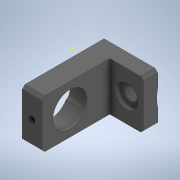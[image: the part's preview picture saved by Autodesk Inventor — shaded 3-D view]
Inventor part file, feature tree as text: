
AUTODESK INVENTOR PART (.ipt)
format: ipt  version: 2020.4 (Build 244396000, 396)  size: 250,880 bytes
history: native  units: in
note: dims shown in document units (in); Inventor stores cm internally (conversion verified against a paired STEP export)
features: sketch x9, extrude x6, hole x3, other x2, chamfer x1
ambient origin geometry x8: Origin, YZ Plane, XZ Plane, XY Plane, X Axis, Y Axis, Z Axis, Center Point
bodies: Solid1 (feature_tree)
feature tree (21):
  other  "Table"
  other  "ADAPTER_fixed-mirror-BH19.05-D12.7"
  extrude  "Extrusion1"  Depth=0.3371in
  sketch  "Sketch2"  dims[d5=0.0in d6=0.6742in]
  extrude  "Extrusion2"  Depth=0.6742in
  extrude  "Extrusion3"  Depth=0.5567in
  extrude  "Extrusion4"  Depth=0.1201in
  hole  "Hole1"  [1 undecoded]
  sketch  "Sketch7"  dims[d15=0.1374in d16=0.0in]
  hole  "Hole2"  [1 undecoded]
  hole  "Hole4"  [1 undecoded]
  extrude  "Extrusion5"  Depth=0.75in
  chamfer  "Chamfer1"  Distance=0.0394in
  extrude  "Extrusion6"  Depth=0.3937in TaperAngle=0.0deg
  sketch  "Sketch10"  dims[d22=0.4774in d23=0.0394in d24=0.0in d25=0.1969in d26=0.0in d27=0.0in d28=0.2362in d29=0.1772in d30=0.2362in d31=0.315in d32=0.0591in d33=90.0deg d34=0.1614in d35=0.0in d36=0.0in d37=0.0in d38=0.1969in d39=0.1969in d40=0.0827in d41=0.2362in d42=0.3126in d43=0.1642in d44=90.0deg d45=0.0827in d46=0.0in d47=0.1378in d48=0.0in d56=0.0849in d57=0.224in d58=0.1575in d59=0.0787in d60=90.0deg d61=0.3492in d62=0.0in d63=0.0413in d64=0.0392in d65=0.0827in d66=0.0in d67=0.0394in d68=0.0787in d69=45.0deg d70=0.0in d71=1.0in d72=0.4862in d73=0.3937in d74=0.0in d75=0.0394in d76=0.0394in d77=0.224in d78=0.0059in d79=0.0098in d80=0.0148in d81=0.5635in d82=0.224in d83=0.8108in d84=0.0025in d85=0.0295in d86=0.0148in]
  sketch  "Sketch1"  dims[d0=0.0in d3=0.3371in]
  sketch  "Sketch3"  dims[d8=0.0in d10=0.5567in]
  sketch  "Sketch5"  dims[d11=0.1201in d12=0.1201in]
  sketch  "Sketch6"  dims[d13=0.75in d14=0.1374in]
  sketch  "Sketch8"  dims[d17=0.0in d18=0.2362in d19=0.0in]
  sketch  "Sketch9"  dims[d20=0.0in d21=0.75in]
note: 3 required parameter values undecoded (feature->parameter linkage not recoverable at this tier; creation-order binding heuristic only, values carry confidence <= 0.55)
